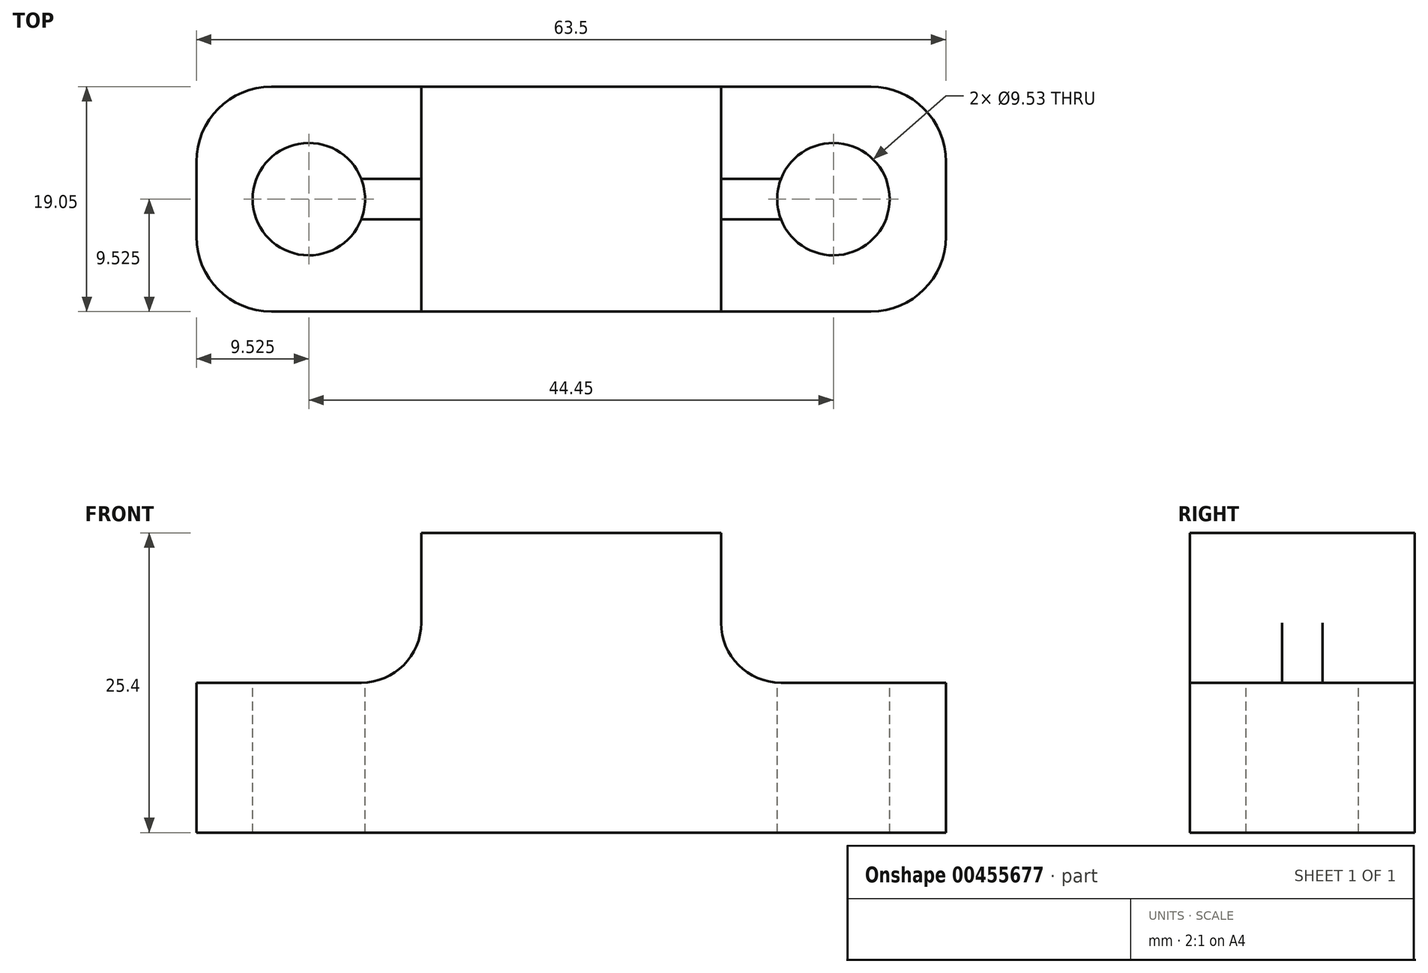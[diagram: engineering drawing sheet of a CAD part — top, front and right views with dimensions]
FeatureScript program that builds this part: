
annotation { "Feature Type Name" : "Feature", "Feature Type Description" : "" }
export const myFeature = defineFeature(function(context is Context, id is Id, definition is map)
    precondition{}
    {
        {
            var Q0;
            Q0=qCreatedBy(makeId("Front.planeOp"),FACE);
            var sketch = newSketch(context, id + "F0", { "sketchPlane" : qUnion([Q0])});
            skLineSegment(sketch, "E0", {"start": v(0, 0) * mm, "end": v(0, 25.4) * mm});
            skLineSegment(sketch, "E1", {"start": v(0, 25.4) * mm, "end": v(-12.7, 25.4) * mm});
            skLineSegment(sketch, "E2", {"start": v(-12.7, 25.4) * mm, "end": v(-12.7, 12.7) * mm});
            skLineSegment(sketch, "E3", {"start": v(-12.7, 12.7) * mm, "end": v(-31.75, 12.7) * mm});
            skLineSegment(sketch, "E4", {"start": v(-31.75, 12.7) * mm, "end": v(-31.75, 0) * mm});
            skLineSegment(sketch, "E5", {"start": v(0, 0) * mm, "end": v(-31.75, 0) * mm});
            skSolve(sketch);
        }
        {
            var Q0;
            Q0=makeQuery(id+"F0.imprint","IMPRINT",FACE,{"disambiguationData":[TD([[makeQuery(id+"F0.imprint","IMPRINT",EDGE,{"derivedFrom":sQuery(id+"F0.wireOp",EDGE,"E0")}),1.0]])]});
            extrude(context, id + "F1", {"entities" : qUnion([Q0]), "depth" : 19.05 * mm});
        }
        {
            var Q0;
            Q0=makeQuery(id+"F1.opExtrude","SWEPT_FACE",FACE,{"disambiguationData":[OSD([sQuery(id+"F0.wireOp",EDGE,"E3")])]});
            var sketch = newSketch(context, id + "F2", { "sketchPlane" : qUnion([Q0])});
            skPoint(sketch, "E6", {"position": v(-22.23, -9.53) * mm});
            skPoint(sketch, "E6.positionSnap0", {"position": v(-22.23, 0) * mm});
            skPoint(sketch, "E6.positionSnap1", {"position": v(-31.75, -9.53) * mm});
            skSolve(sketch);
        }
        {
            var Q0;
            Q0=sQuery(id+"F2.wireOp",VERTEX,"E6");
            var Q1;
            Q1=makeQuery(id+"F1.opExtrude","SWEPT_BODY",BODY,{"disambiguationData":[OSD([sQuery(id+"F0.wireOp",EDGE,"E0"),sQuery(id+"F0.wireOp",EDGE,"E1"),sQuery(id+"F0.wireOp",EDGE,"E2"),sQuery(id+"F0.wireOp",EDGE,"E3"),sQuery(id+"F0.wireOp",EDGE,"E4"),sQuery(id+"F0.wireOp",EDGE,"E5")])]});
            hole(context, id + "F3", {"style" : HoleStyle.SIMPLE, "endStyle" : HoleEndStyle.THROUGH, "holeDiameter" : 9.52 * mm, "isTappedThrough" : true, "tappedDepth" : 12.7 * mm, "tapClearance" : 3, "locations" : qUnion([Q0]), "scope" : qUnion([Q1])});
        }
        {
            var Q0;
            Q0=makeQuery(id+"F1.opExtrude","CAP_EDGE",EDGE,{"disambiguationData":[OSD([sQuery(id+"F0.wireOp",EDGE,"E4")])],"isStart":false});
            var Q1;
            Q1=makeQuery(id+"F1.opExtrude","CAP_EDGE",EDGE,{"disambiguationData":[OSD([sQuery(id+"F0.wireOp",EDGE,"E4")])],"isStart":true});
            fillet(context, id + "F4", {"entities" : qUnion([Q0, Q1]), "radius" : 6.35 * mm, "tangentPropagation" : true, "allowEdgeOverflow" : false});
        }
        {
            var Q0;
            Q0=makeQuery(id+"F1.opExtrude","SWEPT_BODY",BODY,{"disambiguationData":[OSD([sQuery(id+"F0.wireOp",EDGE,"E0"),sQuery(id+"F0.wireOp",EDGE,"E1"),sQuery(id+"F0.wireOp",EDGE,"E2"),sQuery(id+"F0.wireOp",EDGE,"E3"),sQuery(id+"F0.wireOp",EDGE,"E4"),sQuery(id+"F0.wireOp",EDGE,"E5")])]});
            var Q1;
            Q1=makeQuery(id+"F1.opExtrude","SWEPT_FACE",FACE,{"disambiguationData":[OSD([sQuery(id+"F0.wireOp",EDGE,"E0")])]});
            mirror(context, id + "F5", {"operationType" : NewBodyOperationType.ADD, "entities" : qUnion([Q0]), "mirrorPlane" : qUnion([Q1])});
        }
        {
            var Q0;
            Q0=makeQuery(id+"F1.opExtrude","SWEPT_EDGE",EDGE,{"disambiguationData":[OSD([sQuery(id+"F0.wireOp",EDGE,"E2"),sQuery(id+"F0.wireOp",EDGE,"E3")])]});
            var Q1;
            Q1=makeQuery(id+"F5.opPattern","COPY",EDGE,{"derivedFrom":makeQuery(id+"F1.opExtrude","SWEPT_EDGE",EDGE,{"disambiguationData":[OSD([sQuery(id+"F0.wireOp",EDGE,"E2"),sQuery(id+"F0.wireOp",EDGE,"E3")])]}),"instanceName":"1"});
            fillet(context, id + "F6", {"entities" : qUnion([Q0, Q1]), "radius" : 5.08 * mm, "tangentPropagation" : true, "allowEdgeOverflow" : false});
        }
    });
